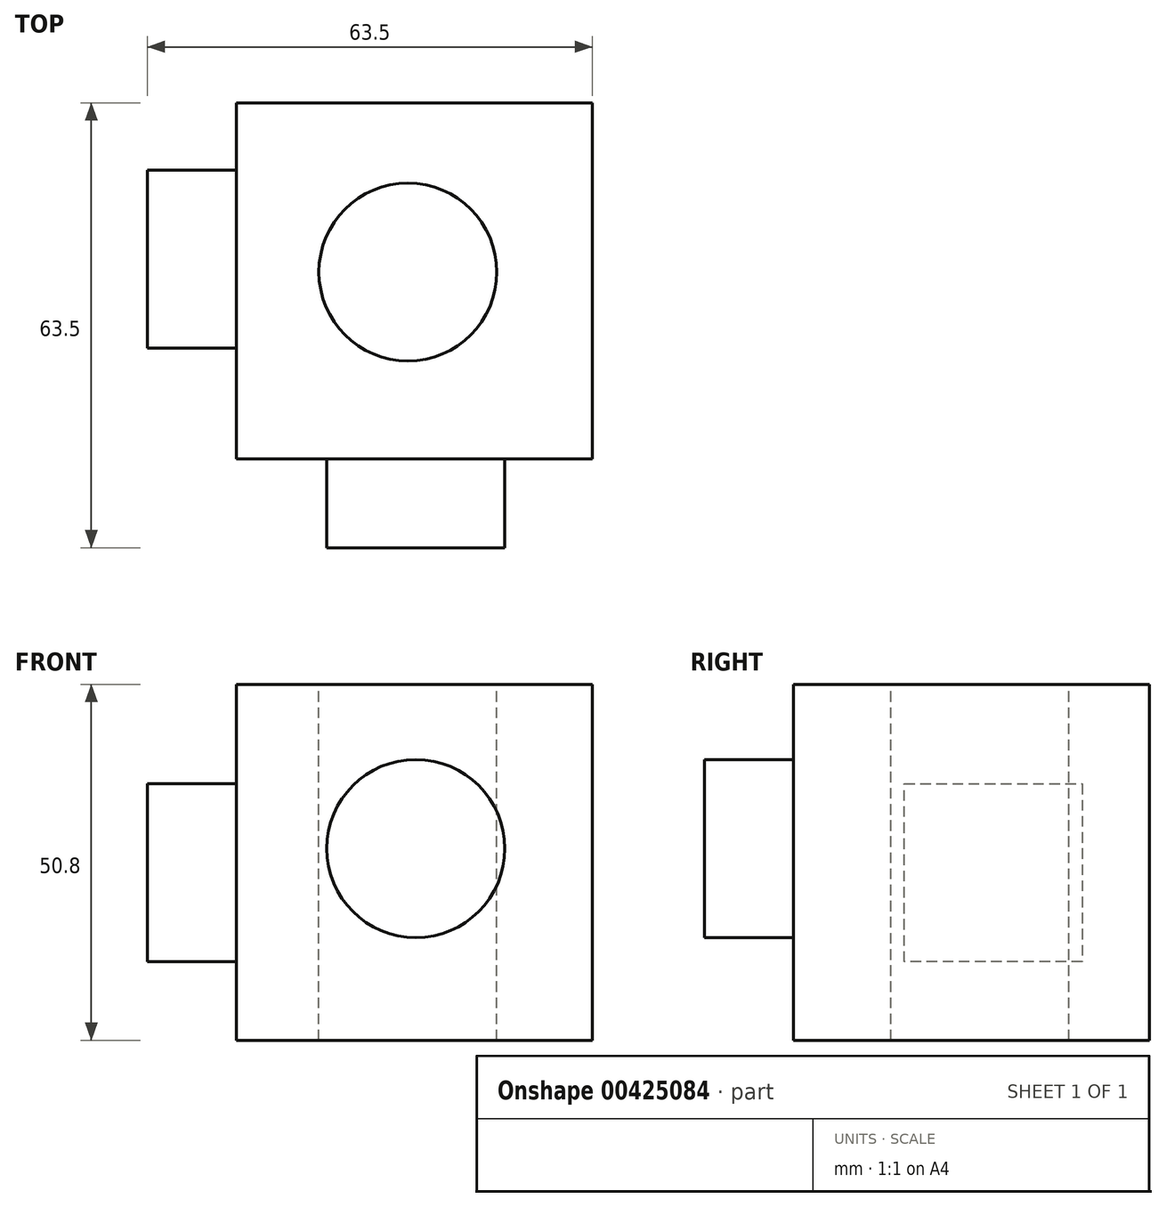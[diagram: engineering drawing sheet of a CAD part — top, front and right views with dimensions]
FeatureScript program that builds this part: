
annotation { "Feature Type Name" : "Feature", "Feature Type Description" : "" }
export const myFeature = defineFeature(function(context is Context, id is Id, definition is map)
    precondition{}
    {
        {
            var Q0;
            Q0=qCreatedBy(makeId("Front.planeOp"),FACE);
            var sketch = newSketch(context, id + "F0", { "sketchPlane" : qUnion([Q0])});
            skLineSegment(sketch, "E0", {"start": v(0, 0) * mm, "end": v(-50.8, 0) * mm});
            skLineSegment(sketch, "E1", {"start": v(-50.8, 0) * mm, "end": v(-50.8, 50.8) * mm});
            skLineSegment(sketch, "E2", {"start": v(-50.8, 50.8) * mm, "end": v(0, 50.8) * mm});
            skLineSegment(sketch, "E3", {"start": v(0, 50.8) * mm, "end": v(0, 0) * mm});
            skSolve(sketch);
        }
        {
            var Q0;
            Q0 = qSketchRegion(id + "F0", true);
            extrude(context, id + "F1", {"entities" : qUnion([Q0]), "depth" : 50.8 * mm});
        }
        {
            var Q0;
            Q0=makeQuery(id+"F1.opExtrude","SWEPT_FACE",FACE,{"disambiguationData":[OSD([sQuery(id+"F0.wireOp",EDGE,"E2")])]});
            var sketch = newSketch(context, id + "F2", { "sketchPlane" : qUnion([Q0])});
            skCircle(sketch, "E4", {"center": v(-26.33, -24.16) * mm, "radius": 12.7 * mm});
            skSolve(sketch);
        }
        {
            var Q0;
            Q0=makeQuery(id+"F2.imprint","IMPRINT",FACE,{"disambiguationData":[TD([[makeQuery(id+"F2.imprint","IMPRINT",EDGE,{"derivedFrom":sQuery(id+"F2.wireOp",EDGE,"E4")}),1.0]])]});
            extrude(context, id + "F3", {"entities" : qUnion([Q0]), "operationType" : NewBodyOperationType.REMOVE, "oppositeDirection" : true, "depth" : 50.8 * mm});
        }
        {
            var Q0;
            Q0=makeQuery(id+"F1.opExtrude","SWEPT_FACE",FACE,{"disambiguationData":[OSD([sQuery(id+"F0.wireOp",EDGE,"E1")])]});
            var sketch = newSketch(context, id + "F4", { "sketchPlane" : qUnion([Q0])});
            skLineSegment(sketch, "E5", {"start": v(9.59, 36.59) * mm, "end": v(9.59, 11.19) * mm});
            skLineSegment(sketch, "E6", {"start": v(9.59, 11.19) * mm, "end": v(34.99, 11.19) * mm});
            skLineSegment(sketch, "E7", {"start": v(34.99, 11.19) * mm, "end": v(34.99, 36.59) * mm});
            skLineSegment(sketch, "E8", {"start": v(34.99, 36.59) * mm, "end": v(9.59, 36.59) * mm});
            skSolve(sketch);
        }
        {
            var Q0;
            Q0 = qSketchRegion(id + "F4", true);
            extrude(context, id + "F5", {"entities" : qUnion([Q0]), "operationType" : NewBodyOperationType.ADD, "depth" : 12.7 * mm});
        }
        {
            var Q0;
            Q0=makeQuery(id+"F1.opExtrude","CAP_FACE",FACE,{"disambiguationData":[OSD([sQuery(id+"F0.wireOp",EDGE,"E0"),sQuery(id+"F0.wireOp",EDGE,"E1"),sQuery(id+"F0.wireOp",EDGE,"E2"),sQuery(id+"F0.wireOp",EDGE,"E3")])],"isStart":false});
            var sketch = newSketch(context, id + "F6", { "sketchPlane" : qUnion([Q0])});
            skCircle(sketch, "E9", {"center": v(-25.2, 27.36) * mm, "radius": 12.7 * mm});
            skSolve(sketch);
        }
        {
            var Q0;
            Q0 = qSketchRegion(id + "F6", true);
            extrude(context, id + "F7", {"entities" : qUnion([Q0]), "operationType" : NewBodyOperationType.ADD, "depth" : 12.7 * mm});
        }
    });
